# Revit family: Landscape-Forms_Hawthorne_Path-Light
name_source: partatom
category: Lighting Fixtures
units: mm (PartAtom-declared; Revit-internal decimal feet)

## family parameters
Always vertical = Yes
Cut with Voids When Loaded = No
Light Source = Yes
OmniClass Number = 23.80.70.14.21
OmniClass Title = Street and Roadway Lighting
Part Type = Normal
Room Calculation Point = No
Round Connector Dimension = Use Diameter
Shared = No
Work Plane-Based = No

## types (1)
- HW140-01
    Apparent Load = 16 VA
    Assembly Code = D5020280
    Color Filter = 16777215
    Default Elevation = 0' - 0"
    Description = Hawthorne Path Light
    Diffuser Lens = LANDSCAPE FORMS - DIFFUSER - ILLUMINATED
    Dimming Lamp Color Temperature Shift = <None>
    Emit Shape Visible in Rendering = No
    Emit from Circle Diameter = 0' - 4"
    Height = 3' - 1"
    Lamp = 12 Cree XHP-E2 LEDs
    Load Classification = Lighting - Exterior
    Manufacturer = Landscape Forms
    Model = HW140-01
    Number of Poles = 1
    Photometric Web File = LF_Hawthorne_HW012L5-40K.ies
    Powdercoat = LANDSCAPE FORMS - POWDERCOATED METAL - NEUTRAL SERIES (BRONZE METALLIC)
    Tilt Angle = 90.00°
    URL = https://www.landscapeforms.com
    Voltage = 120 V
    Wattage Comments = 15.5
